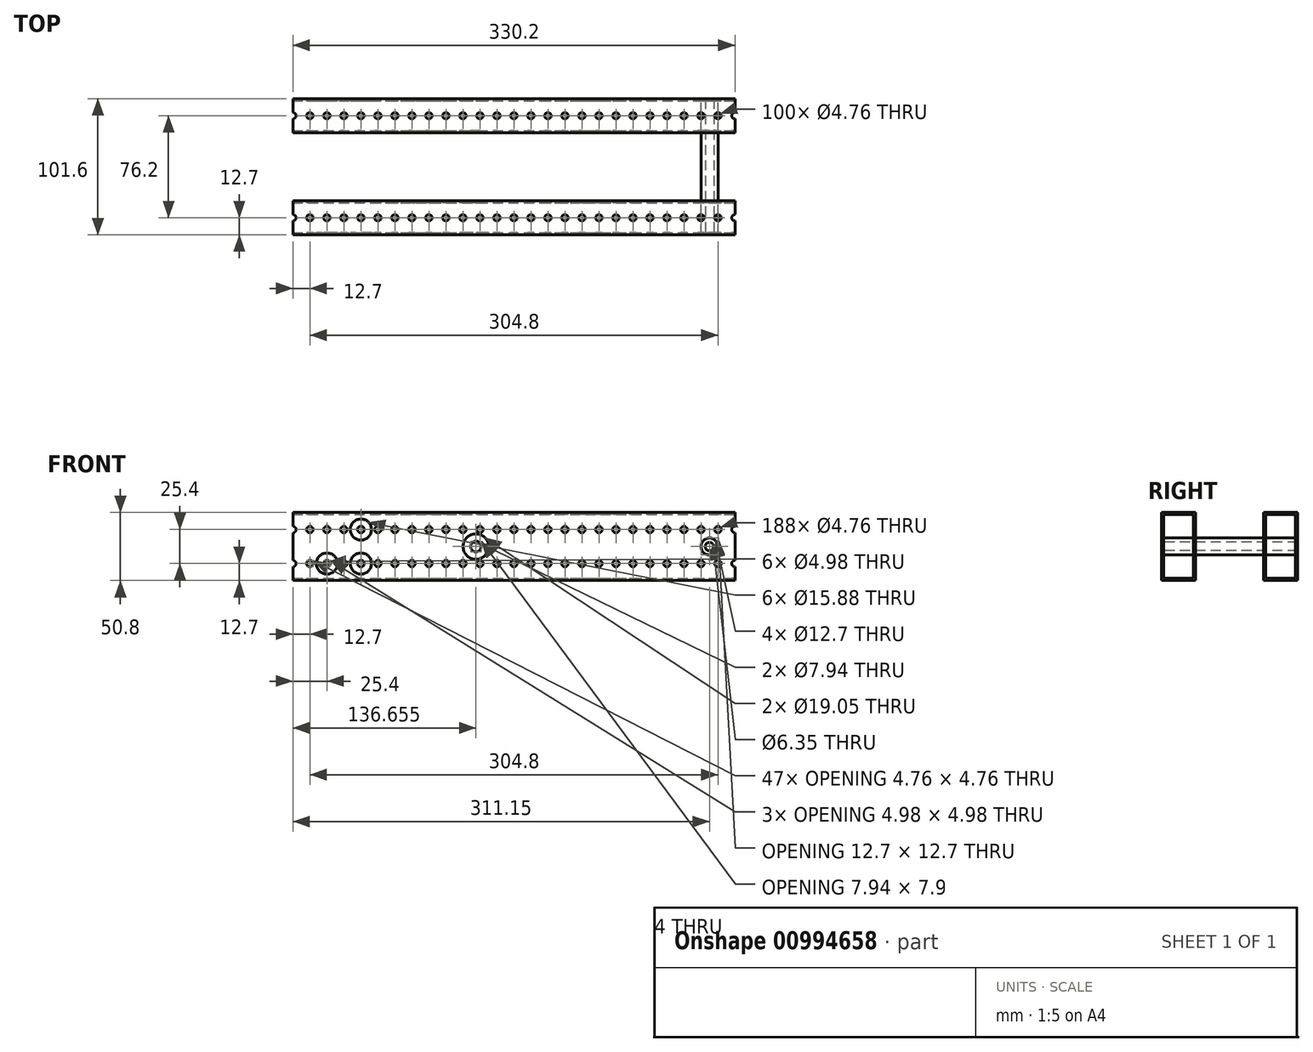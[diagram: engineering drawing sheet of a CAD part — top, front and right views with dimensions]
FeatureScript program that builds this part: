
annotation { "Feature Type Name" : "Feature", "Feature Type Description" : "" }
export const myFeature = defineFeature(function(context is Context, id is Id, definition is map)
    precondition{}
    {
        {
            var Q0;
            Q0=qCreatedBy(makeId("Front.planeOp"),FACE);
            var sketch = newSketch(context, id + "F0", { "sketchPlane" : qUnion([Q0])});
            skLineSegment(sketch, "E0.bottom", {"start": v(0, 0) * mm, "end": v(-330.2, 0) * mm});
            skLineSegment(sketch, "E0.top", {"start": v(0, 50.8) * mm, "end": v(-330.2, 50.8) * mm});
            skLineSegment(sketch, "E0.left", {"start": v(0, 0) * mm, "end": v(0, 50.8) * mm});
            skLineSegment(sketch, "E0.right", {"start": v(-330.2, 0) * mm, "end": v(-330.2, 50.8) * mm});
            skSolve(sketch);
        }
        {
            var Q0;
            Q0=makeQuery(id+"F0.imprint","IMPRINT",FACE,{"disambiguationData":[TD([[makeQuery(id+"F0.imprint","IMPRINT",EDGE,{"derivedFrom":sQuery(id+"F0.wireOp",EDGE,"E0.bottom")}),-1.0]])]});
            extrude(context, id + "F1", {"entities" : qUnion([Q0]), "depth" : 25.4 * mm, "offsetDistance" : 25.4 * mm});
        }
        {
            var Q0;
            Q0=makeQuery(id+"F1.opExtrude","SWEPT_FACE",FACE,{"disambiguationData":[OSD([sQuery(id+"F0.wireOp",EDGE,"E0.left")])]});
            var sketch = newSketch(context, id + "F2", { "sketchPlane" : qUnion([Q0])});
            skLineSegment(sketch, "E1.0", {"start": v(-1.59, 1.59) * mm, "end": v(-1.59, 49.21) * mm});
            skLineSegment(sketch, "E1.1", {"start": v(-23.81, 1.59) * mm, "end": v(-1.59, 1.59) * mm});
            skLineSegment(sketch, "E1.2", {"start": v(-23.81, 49.21) * mm, "end": v(-23.81, 1.59) * mm});
            skLineSegment(sketch, "E1.3", {"start": v(-1.59, 49.21) * mm, "end": v(-23.81, 49.21) * mm});
            skSolve(sketch);
        }
        {
            var Q0;
            Q0 = qSketchRegion(id + "F2", true);
            extrude(context, id + "F3", {"entities" : qUnion([Q0]), "operationType" : NewBodyOperationType.REMOVE, "endBound" : BoundingType.THROUGH_ALL, "oppositeDirection" : true, "depth" : 25.4 * mm, "offsetDistance" : 25.4 * mm});
        }
        {
            var Q0;
            Q0=makeQuery(id+"F1.opExtrude","CAP_FACE",FACE,{"disambiguationData":[OSD([sQuery(id+"F0.wireOp",EDGE,"E0.bottom"),sQuery(id+"F0.wireOp",EDGE,"E0.top"),sQuery(id+"F0.wireOp",EDGE,"E0.left"),sQuery(id+"F0.wireOp",EDGE,"E0.right")])],"isStart":false});
            var sketch = newSketch(context, id + "F4", { "sketchPlane" : qUnion([Q0])});
            skCircle(sketch, "E2", {"center": v(0, 38.1) * mm, "radius": 2.38 * mm});
            skCircle(sketch, "E3", {"center": v(0, 12.7) * mm, "radius": 2.38 * mm});
            skCircle(sketch, "E4.1.0.0", {"center": v(-12.7, 38.1) * mm, "radius": 2.38 * mm});
            skCircle(sketch, "E4.1.0.1", {"center": v(-12.7, 12.7) * mm, "radius": 2.38 * mm});
            skCircle(sketch, "E4.2.0.0", {"center": v(-25.4, 38.1) * mm, "radius": 2.38 * mm});
            skCircle(sketch, "E4.2.0.1", {"center": v(-25.4, 12.7) * mm, "radius": 2.38 * mm});
            skCircle(sketch, "E4.3.0.0", {"center": v(-38.1, 38.1) * mm, "radius": 2.38 * mm});
            skCircle(sketch, "E4.3.0.1", {"center": v(-38.1, 12.7) * mm, "radius": 2.38 * mm});
            skCircle(sketch, "E4.4.0.0", {"center": v(-50.8, 38.1) * mm, "radius": 2.38 * mm});
            skCircle(sketch, "E4.4.0.1", {"center": v(-50.8, 12.7) * mm, "radius": 2.38 * mm});
            skCircle(sketch, "E4.5.0.0", {"center": v(-63.5, 38.1) * mm, "radius": 2.38 * mm});
            skCircle(sketch, "E4.5.0.1", {"center": v(-63.5, 12.7) * mm, "radius": 2.38 * mm});
            skCircle(sketch, "E4.6.0.0", {"center": v(-76.2, 38.1) * mm, "radius": 2.38 * mm});
            skCircle(sketch, "E4.6.0.1", {"center": v(-76.2, 12.7) * mm, "radius": 2.38 * mm});
            skCircle(sketch, "E4.7.0.0", {"center": v(-88.9, 38.1) * mm, "radius": 2.38 * mm});
            skCircle(sketch, "E4.7.0.1", {"center": v(-88.9, 12.7) * mm, "radius": 2.38 * mm});
            skCircle(sketch, "E4.8.0.0", {"center": v(-101.6, 38.1) * mm, "radius": 2.38 * mm});
            skCircle(sketch, "E4.8.0.1", {"center": v(-101.6, 12.7) * mm, "radius": 2.38 * mm});
            skCircle(sketch, "E4.9.0.0", {"center": v(-114.3, 38.1) * mm, "radius": 2.38 * mm});
            skCircle(sketch, "E4.9.0.1", {"center": v(-114.3, 12.7) * mm, "radius": 2.38 * mm});
            skCircle(sketch, "E4.10.0.0", {"center": v(-127, 38.1) * mm, "radius": 2.38 * mm});
            skCircle(sketch, "E4.10.0.1", {"center": v(-127, 12.7) * mm, "radius": 2.38 * mm});
            skCircle(sketch, "E4.11.0.0", {"center": v(-139.7, 38.1) * mm, "radius": 2.38 * mm});
            skCircle(sketch, "E4.11.0.1", {"center": v(-139.7, 12.7) * mm, "radius": 2.38 * mm});
            skCircle(sketch, "E4.12.0.0", {"center": v(-152.4, 38.1) * mm, "radius": 2.38 * mm});
            skCircle(sketch, "E4.12.0.1", {"center": v(-152.4, 12.7) * mm, "radius": 2.38 * mm});
            skCircle(sketch, "E4.13.0.0", {"center": v(-165.1, 38.1) * mm, "radius": 2.38 * mm});
            skCircle(sketch, "E4.13.0.1", {"center": v(-165.1, 12.7) * mm, "radius": 2.38 * mm});
            skCircle(sketch, "E4.14.0.0", {"center": v(-177.8, 38.1) * mm, "radius": 2.38 * mm});
            skCircle(sketch, "E4.14.0.1", {"center": v(-177.8, 12.7) * mm, "radius": 2.38 * mm});
            skCircle(sketch, "E4.15.0.0", {"center": v(-190.5, 38.1) * mm, "radius": 2.38 * mm});
            skCircle(sketch, "E4.15.0.1", {"center": v(-190.5, 12.7) * mm, "radius": 2.38 * mm});
            skCircle(sketch, "E4.16.0.0", {"center": v(-203.2, 38.1) * mm, "radius": 2.38 * mm});
            skCircle(sketch, "E4.16.0.1", {"center": v(-203.2, 12.7) * mm, "radius": 2.38 * mm});
            skCircle(sketch, "E4.17.0.0", {"center": v(-215.9, 38.1) * mm, "radius": 2.38 * mm});
            skCircle(sketch, "E4.17.0.1", {"center": v(-215.9, 12.7) * mm, "radius": 2.38 * mm});
            skCircle(sketch, "E4.18.0.0", {"center": v(-228.6, 38.1) * mm, "radius": 2.38 * mm});
            skCircle(sketch, "E4.18.0.1", {"center": v(-228.6, 12.7) * mm, "radius": 2.38 * mm});
            skCircle(sketch, "E4.19.0.0", {"center": v(-241.3, 38.1) * mm, "radius": 2.38 * mm});
            skCircle(sketch, "E4.19.0.1", {"center": v(-241.3, 12.7) * mm, "radius": 2.38 * mm});
            skCircle(sketch, "E4.20.0.0", {"center": v(-254, 38.1) * mm, "radius": 2.38 * mm});
            skCircle(sketch, "E4.20.0.1", {"center": v(-254, 12.7) * mm, "radius": 2.38 * mm});
            skCircle(sketch, "E4.21.0.0", {"center": v(-266.7, 38.1) * mm, "radius": 2.38 * mm});
            skCircle(sketch, "E4.21.0.1", {"center": v(-266.7, 12.7) * mm, "radius": 2.38 * mm});
            skCircle(sketch, "E4.22.0.0", {"center": v(-279.4, 38.1) * mm, "radius": 2.38 * mm});
            skCircle(sketch, "E4.22.0.1", {"center": v(-279.4, 12.7) * mm, "radius": 2.38 * mm});
            skCircle(sketch, "E4.23.0.0", {"center": v(-292.1, 38.1) * mm, "radius": 2.38 * mm});
            skCircle(sketch, "E4.23.0.1", {"center": v(-292.1, 12.7) * mm, "radius": 2.38 * mm});
            skCircle(sketch, "E4.24.0.0", {"center": v(-304.8, 38.1) * mm, "radius": 2.38 * mm});
            skCircle(sketch, "E4.24.0.1", {"center": v(-304.8, 12.7) * mm, "radius": 2.38 * mm});
            skCircle(sketch, "E4.25.0.0", {"center": v(-317.5, 38.1) * mm, "radius": 2.38 * mm});
            skCircle(sketch, "E4.25.0.1", {"center": v(-317.5, 12.7) * mm, "radius": 2.38 * mm});
            skCircle(sketch, "E4.26.0.0", {"center": v(-330.2, 38.1) * mm, "radius": 2.38 * mm});
            skCircle(sketch, "E4.26.0.1", {"center": v(-330.2, 12.7) * mm, "radius": 2.38 * mm});
            skCircle(sketch, "E4.27.0.0", {"center": v(-342.9, 38.1) * mm, "radius": 2.38 * mm});
            skCircle(sketch, "E4.27.0.1", {"center": v(-342.9, 12.7) * mm, "radius": 2.38 * mm});
            skCircle(sketch, "E4.28.0.0", {"center": v(-355.6, 38.1) * mm, "radius": 2.38 * mm});
            skCircle(sketch, "E4.28.0.1", {"center": v(-355.6, 12.7) * mm, "radius": 2.38 * mm});
            skCircle(sketch, "E4.29.0.0", {"center": v(-368.3, 38.1) * mm, "radius": 2.38 * mm});
            skCircle(sketch, "E4.29.0.1", {"center": v(-368.3, 12.7) * mm, "radius": 2.38 * mm});
            skCircle(sketch, "E4.30.0.0", {"center": v(-381, 38.1) * mm, "radius": 2.38 * mm});
            skCircle(sketch, "E4.30.0.1", {"center": v(-381, 12.7) * mm, "radius": 2.38 * mm});
            skCircle(sketch, "E4.31.0.0", {"center": v(-393.7, 38.1) * mm, "radius": 2.38 * mm});
            skCircle(sketch, "E4.31.0.1", {"center": v(-393.7, 12.7) * mm, "radius": 2.38 * mm});
            skCircle(sketch, "E4.32.0.0", {"center": v(-406.4, 38.1) * mm, "radius": 2.38 * mm});
            skCircle(sketch, "E4.32.0.1", {"center": v(-406.4, 12.7) * mm, "radius": 2.38 * mm});
            skCircle(sketch, "E4.33.0.0", {"center": v(-419.1, 38.1) * mm, "radius": 2.38 * mm});
            skCircle(sketch, "E4.33.0.1", {"center": v(-419.1, 12.7) * mm, "radius": 2.38 * mm});
            skCircle(sketch, "E4.34.0.0", {"center": v(-431.8, 38.1) * mm, "radius": 2.38 * mm});
            skCircle(sketch, "E4.34.0.1", {"center": v(-431.8, 12.7) * mm, "radius": 2.38 * mm});
            skCircle(sketch, "E4.35.0.0", {"center": v(-444.5, 38.1) * mm, "radius": 2.38 * mm});
            skCircle(sketch, "E4.35.0.1", {"center": v(-444.5, 12.7) * mm, "radius": 2.38 * mm});
            skCircle(sketch, "E4.36.0.0", {"center": v(-457.2, 38.1) * mm, "radius": 2.38 * mm});
            skCircle(sketch, "E4.36.0.1", {"center": v(-457.2, 12.7) * mm, "radius": 2.38 * mm});
            skCircle(sketch, "E4.37.0.0", {"center": v(-469.9, 38.1) * mm, "radius": 2.38 * mm});
            skCircle(sketch, "E4.37.0.1", {"center": v(-469.9, 12.7) * mm, "radius": 2.38 * mm});
            skCircle(sketch, "E4.38.0.0", {"center": v(-482.6, 38.1) * mm, "radius": 2.38 * mm});
            skCircle(sketch, "E4.38.0.1", {"center": v(-482.6, 12.7) * mm, "radius": 2.38 * mm});
            skCircle(sketch, "E4.39.0.0", {"center": v(-495.3, 38.1) * mm, "radius": 2.38 * mm});
            skCircle(sketch, "E4.39.0.1", {"center": v(-495.3, 12.7) * mm, "radius": 2.38 * mm});
            skCircle(sketch, "E4.40.0.0", {"center": v(-508, 38.1) * mm, "radius": 2.38 * mm});
            skCircle(sketch, "E4.40.0.1", {"center": v(-508, 12.7) * mm, "radius": 2.38 * mm});
            skCircle(sketch, "E4.41.0.0", {"center": v(-520.7, 38.1) * mm, "radius": 2.38 * mm});
            skCircle(sketch, "E4.41.0.1", {"center": v(-520.7, 12.7) * mm, "radius": 2.38 * mm});
            skCircle(sketch, "E4.42.0.0", {"center": v(-533.4, 38.1) * mm, "radius": 2.38 * mm});
            skCircle(sketch, "E4.42.0.1", {"center": v(-533.4, 12.7) * mm, "radius": 2.38 * mm});
            skCircle(sketch, "E4.43.0.0", {"center": v(-546.1, 38.1) * mm, "radius": 2.38 * mm});
            skCircle(sketch, "E4.43.0.1", {"center": v(-546.1, 12.7) * mm, "radius": 2.38 * mm});
            skCircle(sketch, "E4.44.0.0", {"center": v(-558.8, 38.1) * mm, "radius": 2.38 * mm});
            skCircle(sketch, "E4.44.0.1", {"center": v(-558.8, 12.7) * mm, "radius": 2.38 * mm});
            skCircle(sketch, "E4.45.0.0", {"center": v(-571.5, 38.1) * mm, "radius": 2.38 * mm});
            skCircle(sketch, "E4.45.0.1", {"center": v(-571.5, 12.7) * mm, "radius": 2.38 * mm});
            skCircle(sketch, "E4.46.0.0", {"center": v(-584.2, 38.1) * mm, "radius": 2.38 * mm});
            skCircle(sketch, "E4.46.0.1", {"center": v(-584.2, 12.7) * mm, "radius": 2.38 * mm});
            skCircle(sketch, "E4.47.0.0", {"center": v(-596.9, 38.1) * mm, "radius": 2.38 * mm});
            skCircle(sketch, "E4.47.0.1", {"center": v(-596.9, 12.7) * mm, "radius": 2.38 * mm});
            skCircle(sketch, "E4.48.0.0", {"center": v(-609.6, 38.1) * mm, "radius": 2.38 * mm});
            skCircle(sketch, "E4.48.0.1", {"center": v(-609.6, 12.7) * mm, "radius": 2.38 * mm});
            skCircle(sketch, "E4.49.0.0", {"center": v(-622.3, 38.1) * mm, "radius": 2.38 * mm});
            skCircle(sketch, "E4.49.0.1", {"center": v(-622.3, 12.7) * mm, "radius": 2.38 * mm});
            skCircle(sketch, "E4.50.0.0", {"center": v(-635, 38.1) * mm, "radius": 2.38 * mm});
            skCircle(sketch, "E4.50.0.1", {"center": v(-635, 12.7) * mm, "radius": 2.38 * mm});
            skCircle(sketch, "E4.51.0.0", {"center": v(-647.7, 38.1) * mm, "radius": 2.38 * mm});
            skCircle(sketch, "E4.51.0.1", {"center": v(-647.7, 12.7) * mm, "radius": 2.38 * mm});
            skCircle(sketch, "E4.52.0.0", {"center": v(-660.4, 38.1) * mm, "radius": 2.38 * mm});
            skCircle(sketch, "E4.52.0.1", {"center": v(-660.4, 12.7) * mm, "radius": 2.38 * mm});
            skCircle(sketch, "E4.53.0.0", {"center": v(-673.1, 38.1) * mm, "radius": 2.38 * mm});
            skCircle(sketch, "E4.53.0.1", {"center": v(-673.1, 12.7) * mm, "radius": 2.38 * mm});
            skCircle(sketch, "E4.54.0.0", {"center": v(-685.8, 38.1) * mm, "radius": 2.38 * mm});
            skCircle(sketch, "E4.54.0.1", {"center": v(-685.8, 12.7) * mm, "radius": 2.38 * mm});
            skCircle(sketch, "E4.55.0.0", {"center": v(-698.5, 38.1) * mm, "radius": 2.38 * mm});
            skCircle(sketch, "E4.55.0.1", {"center": v(-698.5, 12.7) * mm, "radius": 2.38 * mm});
            skCircle(sketch, "E4.56.0.0", {"center": v(-711.2, 38.1) * mm, "radius": 2.38 * mm});
            skCircle(sketch, "E4.56.0.1", {"center": v(-711.2, 12.7) * mm, "radius": 2.38 * mm});
            skCircle(sketch, "E4.57.0.0", {"center": v(-723.9, 38.1) * mm, "radius": 2.38 * mm});
            skCircle(sketch, "E4.57.0.1", {"center": v(-723.9, 12.7) * mm, "radius": 2.38 * mm});
            skCircle(sketch, "E4.58.0.0", {"center": v(-736.6, 38.1) * mm, "radius": 2.38 * mm});
            skCircle(sketch, "E4.58.0.1", {"center": v(-736.6, 12.7) * mm, "radius": 2.38 * mm});
            skCircle(sketch, "E4.59.0.0", {"center": v(-749.3, 38.1) * mm, "radius": 2.38 * mm});
            skCircle(sketch, "E4.59.0.1", {"center": v(-749.3, 12.7) * mm, "radius": 2.38 * mm});
            skCircle(sketch, "E4.60.0.0", {"center": v(-762, 38.1) * mm, "radius": 2.38 * mm});
            skCircle(sketch, "E4.60.0.1", {"center": v(-762, 12.7) * mm, "radius": 2.38 * mm});
            skCircle(sketch, "E4.61.0.0", {"center": v(-774.7, 38.1) * mm, "radius": 2.38 * mm});
            skCircle(sketch, "E4.61.0.1", {"center": v(-774.7, 12.7) * mm, "radius": 2.38 * mm});
            skCircle(sketch, "E4.62.0.0", {"center": v(-787.4, 38.1) * mm, "radius": 2.38 * mm});
            skCircle(sketch, "E4.62.0.1", {"center": v(-787.4, 12.7) * mm, "radius": 2.38 * mm});
            skCircle(sketch, "E4.63.0.0", {"center": v(-800.1, 38.1) * mm, "radius": 2.38 * mm});
            skCircle(sketch, "E4.63.0.1", {"center": v(-800.1, 12.7) * mm, "radius": 2.38 * mm});
            skCircle(sketch, "E4.64.0.0", {"center": v(-812.8, 38.1) * mm, "radius": 2.38 * mm});
            skCircle(sketch, "E4.64.0.1", {"center": v(-812.8, 12.7) * mm, "radius": 2.38 * mm});
            skCircle(sketch, "E4.65.0.0", {"center": v(-825.5, 38.1) * mm, "radius": 2.38 * mm});
            skCircle(sketch, "E4.65.0.1", {"center": v(-825.5, 12.7) * mm, "radius": 2.38 * mm});
            skCircle(sketch, "E4.66.0.0", {"center": v(-838.2, 38.1) * mm, "radius": 2.38 * mm});
            skCircle(sketch, "E4.66.0.1", {"center": v(-838.2, 12.7) * mm, "radius": 2.38 * mm});
            skCircle(sketch, "E4.67.0.0", {"center": v(-850.9, 38.1) * mm, "radius": 2.38 * mm});
            skCircle(sketch, "E4.67.0.1", {"center": v(-850.9, 12.7) * mm, "radius": 2.38 * mm});
            skCircle(sketch, "E4.68.0.0", {"center": v(-863.6, 38.1) * mm, "radius": 2.38 * mm});
            skCircle(sketch, "E4.68.0.1", {"center": v(-863.6, 12.7) * mm, "radius": 2.38 * mm});
            skCircle(sketch, "E4.69.0.0", {"center": v(-876.3, 38.1) * mm, "radius": 2.38 * mm});
            skCircle(sketch, "E4.69.0.1", {"center": v(-876.3, 12.7) * mm, "radius": 2.38 * mm});
            skCircle(sketch, "E4.70.0.0", {"center": v(-889, 38.1) * mm, "radius": 2.38 * mm});
            skCircle(sketch, "E4.70.0.1", {"center": v(-889, 12.7) * mm, "radius": 2.38 * mm});
            skCircle(sketch, "E4.71.0.0", {"center": v(-901.7, 38.1) * mm, "radius": 2.38 * mm});
            skCircle(sketch, "E4.71.0.1", {"center": v(-901.7, 12.7) * mm, "radius": 2.38 * mm});
            skCircle(sketch, "E4.72.0.0", {"center": v(-914.4, 38.1) * mm, "radius": 2.38 * mm});
            skCircle(sketch, "E4.72.0.1", {"center": v(-914.4, 12.7) * mm, "radius": 2.38 * mm});
            skCircle(sketch, "E4.73.0.0", {"center": v(-927.1, 38.1) * mm, "radius": 2.38 * mm});
            skCircle(sketch, "E4.73.0.1", {"center": v(-927.1, 12.7) * mm, "radius": 2.38 * mm});
            skCircle(sketch, "E4.74.0.0", {"center": v(-939.8, 38.1) * mm, "radius": 2.38 * mm});
            skCircle(sketch, "E4.74.0.1", {"center": v(-939.8, 12.7) * mm, "radius": 2.38 * mm});
            skCircle(sketch, "E4.75.0.0", {"center": v(-952.5, 38.1) * mm, "radius": 2.38 * mm});
            skCircle(sketch, "E4.75.0.1", {"center": v(-952.5, 12.7) * mm, "radius": 2.38 * mm});
            skCircle(sketch, "E4.76.0.0", {"center": v(-965.2, 38.1) * mm, "radius": 2.38 * mm});
            skCircle(sketch, "E4.76.0.1", {"center": v(-965.2, 12.7) * mm, "radius": 2.38 * mm});
            skCircle(sketch, "E4.77.0.0", {"center": v(-977.9, 38.1) * mm, "radius": 2.38 * mm});
            skCircle(sketch, "E4.77.0.1", {"center": v(-977.9, 12.7) * mm, "radius": 2.38 * mm});
            skCircle(sketch, "E4.78.0.0", {"center": v(-990.6, 38.1) * mm, "radius": 2.38 * mm});
            skCircle(sketch, "E4.78.0.1", {"center": v(-990.6, 12.7) * mm, "radius": 2.38 * mm});
            skCircle(sketch, "E4.79.0.0", {"center": v(-1003.3, 38.1) * mm, "radius": 2.38 * mm});
            skCircle(sketch, "E4.79.0.1", {"center": v(-1003.3, 12.7) * mm, "radius": 2.38 * mm});
            skCircle(sketch, "E4.80.0.0", {"center": v(-1016, 38.1) * mm, "radius": 2.38 * mm});
            skCircle(sketch, "E4.80.0.1", {"center": v(-1016, 12.7) * mm, "radius": 2.38 * mm});
            skCircle(sketch, "E4.81.0.0", {"center": v(-1028.7, 38.1) * mm, "radius": 2.38 * mm});
            skCircle(sketch, "E4.81.0.1", {"center": v(-1028.7, 12.7) * mm, "radius": 2.38 * mm});
            skCircle(sketch, "E4.82.0.0", {"center": v(-1041.4, 38.1) * mm, "radius": 2.38 * mm});
            skCircle(sketch, "E4.82.0.1", {"center": v(-1041.4, 12.7) * mm, "radius": 2.38 * mm});
            skCircle(sketch, "E4.83.0.0", {"center": v(-1054.1, 38.1) * mm, "radius": 2.38 * mm});
            skCircle(sketch, "E4.83.0.1", {"center": v(-1054.1, 12.7) * mm, "radius": 2.38 * mm});
            skCircle(sketch, "E4.84.0.0", {"center": v(-1066.8, 38.1) * mm, "radius": 2.38 * mm});
            skCircle(sketch, "E4.84.0.1", {"center": v(-1066.8, 12.7) * mm, "radius": 2.38 * mm});
            skCircle(sketch, "E4.85.0.0", {"center": v(-1079.5, 38.1) * mm, "radius": 2.38 * mm});
            skCircle(sketch, "E4.85.0.1", {"center": v(-1079.5, 12.7) * mm, "radius": 2.38 * mm});
            skCircle(sketch, "E4.86.0.0", {"center": v(-1092.2, 38.1) * mm, "radius": 2.38 * mm});
            skCircle(sketch, "E4.86.0.1", {"center": v(-1092.2, 12.7) * mm, "radius": 2.38 * mm});
            skCircle(sketch, "E4.87.0.0", {"center": v(-1104.9, 38.1) * mm, "radius": 2.38 * mm});
            skCircle(sketch, "E4.87.0.1", {"center": v(-1104.9, 12.7) * mm, "radius": 2.38 * mm});
            skCircle(sketch, "E4.88.0.0", {"center": v(-1117.6, 38.1) * mm, "radius": 2.38 * mm});
            skCircle(sketch, "E4.88.0.1", {"center": v(-1117.6, 12.7) * mm, "radius": 2.38 * mm});
            skCircle(sketch, "E4.89.0.0", {"center": v(-1130.3, 38.1) * mm, "radius": 2.38 * mm});
            skCircle(sketch, "E4.89.0.1", {"center": v(-1130.3, 12.7) * mm, "radius": 2.38 * mm});
            skCircle(sketch, "E4.90.0.0", {"center": v(-1143, 38.1) * mm, "radius": 2.38 * mm});
            skCircle(sketch, "E4.90.0.1", {"center": v(-1143, 12.7) * mm, "radius": 2.38 * mm});
            skCircle(sketch, "E4.91.0.0", {"center": v(-1155.7, 38.1) * mm, "radius": 2.38 * mm});
            skCircle(sketch, "E4.91.0.1", {"center": v(-1155.7, 12.7) * mm, "radius": 2.38 * mm});
            skCircle(sketch, "E4.92.0.0", {"center": v(-1168.4, 38.1) * mm, "radius": 2.38 * mm});
            skCircle(sketch, "E4.92.0.1", {"center": v(-1168.4, 12.7) * mm, "radius": 2.38 * mm});
            skCircle(sketch, "E4.93.0.0", {"center": v(-1181.1, 38.1) * mm, "radius": 2.38 * mm});
            skCircle(sketch, "E4.93.0.1", {"center": v(-1181.1, 12.7) * mm, "radius": 2.38 * mm});
            skCircle(sketch, "E4.94.0.0", {"center": v(-1193.8, 38.1) * mm, "radius": 2.38 * mm});
            skCircle(sketch, "E4.94.0.1", {"center": v(-1193.8, 12.7) * mm, "radius": 2.38 * mm});
            skCircle(sketch, "E4.95.0.0", {"center": v(-1206.5, 38.1) * mm, "radius": 2.38 * mm});
            skCircle(sketch, "E4.95.0.1", {"center": v(-1206.5, 12.7) * mm, "radius": 2.38 * mm});
            skCircle(sketch, "E4.96.0.0", {"center": v(-1219.2, 38.1) * mm, "radius": 2.38 * mm});
            skCircle(sketch, "E4.96.0.1", {"center": v(-1219.2, 12.7) * mm, "radius": 2.38 * mm});
            skCircle(sketch, "E4.97.0.0", {"center": v(-1231.9, 38.1) * mm, "radius": 2.38 * mm});
            skCircle(sketch, "E4.97.0.1", {"center": v(-1231.9, 12.7) * mm, "radius": 2.38 * mm});
            skCircle(sketch, "E4.98.0.0", {"center": v(-1244.6, 38.1) * mm, "radius": 2.38 * mm});
            skCircle(sketch, "E4.98.0.1", {"center": v(-1244.6, 12.7) * mm, "radius": 2.38 * mm});
            skCircle(sketch, "E4.99.0.0", {"center": v(-1257.3, 38.1) * mm, "radius": 2.38 * mm});
            skCircle(sketch, "E4.99.0.1", {"center": v(-1257.3, 12.7) * mm, "radius": 2.38 * mm});
            skLineSegment(sketch, "E4.direction1", {"start": v(0, 12.7) * mm, "end": v(-12.7, 12.7) * mm, "construction": true});
            skSolve(sketch);
        }
        {
            var Q0;
            Q0 = qSketchRegion(id + "F4", true);
            extrude(context, id + "F5", {"entities" : qUnion([Q0]), "operationType" : NewBodyOperationType.REMOVE, "endBound" : BoundingType.THROUGH_ALL, "oppositeDirection" : true, "depth" : 25.4 * mm, "offsetDistance" : 25.4 * mm});
        }
        {
            var Q0;
            Q0=makeQuery(id+"F1.opExtrude","SWEPT_FACE",FACE,{"disambiguationData":[OSD([sQuery(id+"F0.wireOp",EDGE,"E0.top")])]});
            var sketch = newSketch(context, id + "F6", { "sketchPlane" : qUnion([Q0])});
            skCircle(sketch, "E5", {"center": v(0, -12.7) * mm, "radius": 2.38 * mm});
            skCircle(sketch, "E6.1.0.0", {"center": v(-12.7, -12.7) * mm, "radius": 2.38 * mm});
            skCircle(sketch, "E6.2.0.0", {"center": v(-25.4, -12.7) * mm, "radius": 2.38 * mm});
            skCircle(sketch, "E6.3.0.0", {"center": v(-38.1, -12.7) * mm, "radius": 2.38 * mm});
            skCircle(sketch, "E6.4.0.0", {"center": v(-50.8, -12.7) * mm, "radius": 2.38 * mm});
            skCircle(sketch, "E6.5.0.0", {"center": v(-63.5, -12.7) * mm, "radius": 2.38 * mm});
            skCircle(sketch, "E6.6.0.0", {"center": v(-76.2, -12.7) * mm, "radius": 2.38 * mm});
            skCircle(sketch, "E6.7.0.0", {"center": v(-88.9, -12.7) * mm, "radius": 2.38 * mm});
            skCircle(sketch, "E6.8.0.0", {"center": v(-101.6, -12.7) * mm, "radius": 2.38 * mm});
            skCircle(sketch, "E6.9.0.0", {"center": v(-114.3, -12.7) * mm, "radius": 2.38 * mm});
            skCircle(sketch, "E6.10.0.0", {"center": v(-127, -12.7) * mm, "radius": 2.38 * mm});
            skCircle(sketch, "E6.11.0.0", {"center": v(-139.7, -12.7) * mm, "radius": 2.38 * mm});
            skCircle(sketch, "E6.12.0.0", {"center": v(-152.4, -12.7) * mm, "radius": 2.38 * mm});
            skCircle(sketch, "E6.13.0.0", {"center": v(-165.1, -12.7) * mm, "radius": 2.38 * mm});
            skCircle(sketch, "E6.14.0.0", {"center": v(-177.8, -12.7) * mm, "radius": 2.38 * mm});
            skCircle(sketch, "E6.15.0.0", {"center": v(-190.5, -12.7) * mm, "radius": 2.38 * mm});
            skCircle(sketch, "E6.16.0.0", {"center": v(-203.2, -12.7) * mm, "radius": 2.38 * mm});
            skCircle(sketch, "E6.17.0.0", {"center": v(-215.9, -12.7) * mm, "radius": 2.38 * mm});
            skCircle(sketch, "E6.18.0.0", {"center": v(-228.6, -12.7) * mm, "radius": 2.38 * mm});
            skCircle(sketch, "E6.19.0.0", {"center": v(-241.3, -12.7) * mm, "radius": 2.38 * mm});
            skCircle(sketch, "E6.20.0.0", {"center": v(-254, -12.7) * mm, "radius": 2.38 * mm});
            skCircle(sketch, "E6.21.0.0", {"center": v(-266.7, -12.7) * mm, "radius": 2.38 * mm});
            skCircle(sketch, "E6.22.0.0", {"center": v(-279.4, -12.7) * mm, "radius": 2.38 * mm});
            skCircle(sketch, "E6.23.0.0", {"center": v(-292.1, -12.7) * mm, "radius": 2.38 * mm});
            skCircle(sketch, "E6.24.0.0", {"center": v(-304.8, -12.7) * mm, "radius": 2.38 * mm});
            skCircle(sketch, "E6.25.0.0", {"center": v(-317.5, -12.7) * mm, "radius": 2.38 * mm});
            skCircle(sketch, "E6.26.0.0", {"center": v(-330.2, -12.7) * mm, "radius": 2.38 * mm});
            skCircle(sketch, "E6.27.0.0", {"center": v(-342.9, -12.7) * mm, "radius": 2.38 * mm});
            skCircle(sketch, "E6.28.0.0", {"center": v(-355.6, -12.7) * mm, "radius": 2.38 * mm});
            skCircle(sketch, "E6.29.0.0", {"center": v(-368.3, -12.7) * mm, "radius": 2.38 * mm});
            skCircle(sketch, "E6.30.0.0", {"center": v(-381, -12.7) * mm, "radius": 2.38 * mm});
            skCircle(sketch, "E6.31.0.0", {"center": v(-393.7, -12.7) * mm, "radius": 2.38 * mm});
            skCircle(sketch, "E6.32.0.0", {"center": v(-406.4, -12.7) * mm, "radius": 2.38 * mm});
            skCircle(sketch, "E6.33.0.0", {"center": v(-419.1, -12.7) * mm, "radius": 2.38 * mm});
            skCircle(sketch, "E6.34.0.0", {"center": v(-431.8, -12.7) * mm, "radius": 2.38 * mm});
            skCircle(sketch, "E6.35.0.0", {"center": v(-444.5, -12.7) * mm, "radius": 2.38 * mm});
            skCircle(sketch, "E6.36.0.0", {"center": v(-457.2, -12.7) * mm, "radius": 2.38 * mm});
            skCircle(sketch, "E6.37.0.0", {"center": v(-469.9, -12.7) * mm, "radius": 2.38 * mm});
            skCircle(sketch, "E6.38.0.0", {"center": v(-482.6, -12.7) * mm, "radius": 2.38 * mm});
            skCircle(sketch, "E6.39.0.0", {"center": v(-495.3, -12.7) * mm, "radius": 2.38 * mm});
            skCircle(sketch, "E6.40.0.0", {"center": v(-508, -12.7) * mm, "radius": 2.38 * mm});
            skCircle(sketch, "E6.41.0.0", {"center": v(-520.7, -12.7) * mm, "radius": 2.38 * mm});
            skCircle(sketch, "E6.42.0.0", {"center": v(-533.4, -12.7) * mm, "radius": 2.38 * mm});
            skCircle(sketch, "E6.43.0.0", {"center": v(-546.1, -12.7) * mm, "radius": 2.38 * mm});
            skCircle(sketch, "E6.44.0.0", {"center": v(-558.8, -12.7) * mm, "radius": 2.38 * mm});
            skCircle(sketch, "E6.45.0.0", {"center": v(-571.5, -12.7) * mm, "radius": 2.38 * mm});
            skCircle(sketch, "E6.46.0.0", {"center": v(-584.2, -12.7) * mm, "radius": 2.38 * mm});
            skCircle(sketch, "E6.47.0.0", {"center": v(-596.9, -12.7) * mm, "radius": 2.38 * mm});
            skCircle(sketch, "E6.48.0.0", {"center": v(-609.6, -12.7) * mm, "radius": 2.38 * mm});
            skCircle(sketch, "E6.49.0.0", {"center": v(-622.3, -12.7) * mm, "radius": 2.38 * mm});
            skCircle(sketch, "E6.50.0.0", {"center": v(-635, -12.7) * mm, "radius": 2.38 * mm});
            skCircle(sketch, "E6.51.0.0", {"center": v(-647.7, -12.7) * mm, "radius": 2.38 * mm});
            skCircle(sketch, "E6.52.0.0", {"center": v(-660.4, -12.7) * mm, "radius": 2.38 * mm});
            skCircle(sketch, "E6.53.0.0", {"center": v(-673.1, -12.7) * mm, "radius": 2.38 * mm});
            skCircle(sketch, "E6.54.0.0", {"center": v(-685.8, -12.7) * mm, "radius": 2.38 * mm});
            skCircle(sketch, "E6.55.0.0", {"center": v(-698.5, -12.7) * mm, "radius": 2.38 * mm});
            skCircle(sketch, "E6.56.0.0", {"center": v(-711.2, -12.7) * mm, "radius": 2.38 * mm});
            skCircle(sketch, "E6.57.0.0", {"center": v(-723.9, -12.7) * mm, "radius": 2.38 * mm});
            skCircle(sketch, "E6.58.0.0", {"center": v(-736.6, -12.7) * mm, "radius": 2.38 * mm});
            skCircle(sketch, "E6.59.0.0", {"center": v(-749.3, -12.7) * mm, "radius": 2.38 * mm});
            skCircle(sketch, "E6.60.0.0", {"center": v(-762, -12.7) * mm, "radius": 2.38 * mm});
            skCircle(sketch, "E6.61.0.0", {"center": v(-774.7, -12.7) * mm, "radius": 2.38 * mm});
            skCircle(sketch, "E6.62.0.0", {"center": v(-787.4, -12.7) * mm, "radius": 2.38 * mm});
            skCircle(sketch, "E6.63.0.0", {"center": v(-800.1, -12.7) * mm, "radius": 2.38 * mm});
            skCircle(sketch, "E6.64.0.0", {"center": v(-812.8, -12.7) * mm, "radius": 2.38 * mm});
            skCircle(sketch, "E6.65.0.0", {"center": v(-825.5, -12.7) * mm, "radius": 2.38 * mm});
            skCircle(sketch, "E6.66.0.0", {"center": v(-838.2, -12.7) * mm, "radius": 2.38 * mm});
            skCircle(sketch, "E6.67.0.0", {"center": v(-850.9, -12.7) * mm, "radius": 2.38 * mm});
            skCircle(sketch, "E6.68.0.0", {"center": v(-863.6, -12.7) * mm, "radius": 2.38 * mm});
            skCircle(sketch, "E6.69.0.0", {"center": v(-876.3, -12.7) * mm, "radius": 2.38 * mm});
            skCircle(sketch, "E6.70.0.0", {"center": v(-889, -12.7) * mm, "radius": 2.38 * mm});
            skCircle(sketch, "E6.71.0.0", {"center": v(-901.7, -12.7) * mm, "radius": 2.38 * mm});
            skCircle(sketch, "E6.72.0.0", {"center": v(-914.4, -12.7) * mm, "radius": 2.38 * mm});
            skCircle(sketch, "E6.73.0.0", {"center": v(-927.1, -12.7) * mm, "radius": 2.38 * mm});
            skCircle(sketch, "E6.74.0.0", {"center": v(-939.8, -12.7) * mm, "radius": 2.38 * mm});
            skCircle(sketch, "E6.75.0.0", {"center": v(-952.5, -12.7) * mm, "radius": 2.38 * mm});
            skCircle(sketch, "E6.76.0.0", {"center": v(-965.2, -12.7) * mm, "radius": 2.38 * mm});
            skCircle(sketch, "E6.77.0.0", {"center": v(-977.9, -12.7) * mm, "radius": 2.38 * mm});
            skCircle(sketch, "E6.78.0.0", {"center": v(-990.6, -12.7) * mm, "radius": 2.38 * mm});
            skCircle(sketch, "E6.79.0.0", {"center": v(-1003.3, -12.7) * mm, "radius": 2.38 * mm});
            skCircle(sketch, "E6.80.0.0", {"center": v(-1016, -12.7) * mm, "radius": 2.38 * mm});
            skCircle(sketch, "E6.81.0.0", {"center": v(-1028.7, -12.7) * mm, "radius": 2.38 * mm});
            skCircle(sketch, "E6.82.0.0", {"center": v(-1041.4, -12.7) * mm, "radius": 2.38 * mm});
            skCircle(sketch, "E6.83.0.0", {"center": v(-1054.1, -12.7) * mm, "radius": 2.38 * mm});
            skCircle(sketch, "E6.84.0.0", {"center": v(-1066.8, -12.7) * mm, "radius": 2.38 * mm});
            skCircle(sketch, "E6.85.0.0", {"center": v(-1079.5, -12.7) * mm, "radius": 2.38 * mm});
            skCircle(sketch, "E6.86.0.0", {"center": v(-1092.2, -12.7) * mm, "radius": 2.38 * mm});
            skCircle(sketch, "E6.87.0.0", {"center": v(-1104.9, -12.7) * mm, "radius": 2.38 * mm});
            skCircle(sketch, "E6.88.0.0", {"center": v(-1117.6, -12.7) * mm, "radius": 2.38 * mm});
            skCircle(sketch, "E6.89.0.0", {"center": v(-1130.3, -12.7) * mm, "radius": 2.38 * mm});
            skCircle(sketch, "E6.90.0.0", {"center": v(-1143, -12.7) * mm, "radius": 2.38 * mm});
            skCircle(sketch, "E6.91.0.0", {"center": v(-1155.7, -12.7) * mm, "radius": 2.38 * mm});
            skCircle(sketch, "E6.92.0.0", {"center": v(-1168.4, -12.7) * mm, "radius": 2.38 * mm});
            skCircle(sketch, "E6.93.0.0", {"center": v(-1181.1, -12.7) * mm, "radius": 2.38 * mm});
            skCircle(sketch, "E6.94.0.0", {"center": v(-1193.8, -12.7) * mm, "radius": 2.38 * mm});
            skCircle(sketch, "E6.95.0.0", {"center": v(-1206.5, -12.7) * mm, "radius": 2.38 * mm});
            skCircle(sketch, "E6.96.0.0", {"center": v(-1219.2, -12.7) * mm, "radius": 2.38 * mm});
            skCircle(sketch, "E6.97.0.0", {"center": v(-1231.9, -12.7) * mm, "radius": 2.38 * mm});
            skCircle(sketch, "E6.98.0.0", {"center": v(-1244.6, -12.7) * mm, "radius": 2.38 * mm});
            skCircle(sketch, "E6.99.0.0", {"center": v(-1257.3, -12.7) * mm, "radius": 2.38 * mm});
            skLineSegment(sketch, "E6.direction1", {"start": v(0, -12.7) * mm, "end": v(-12.7, -12.7) * mm, "construction": true});
            skSolve(sketch);
        }
        {
            var Q0;
            Q0 = qSketchRegion(id + "F6", true);
            extrude(context, id + "F7", {"entities" : qUnion([Q0]), "operationType" : NewBodyOperationType.REMOVE, "endBound" : BoundingType.THROUGH_ALL, "oppositeDirection" : true, "depth" : 25.4 * mm, "offsetDistance" : 25.4 * mm});
        }
        {
            var Q0;
            Q0=makeQuery(id+"F1.opExtrude","CAP_FACE",FACE,{"disambiguationData":[OSD([sQuery(id+"F0.wireOp",EDGE,"E0.bottom"),sQuery(id+"F0.wireOp",EDGE,"E0.top"),sQuery(id+"F0.wireOp",EDGE,"E0.left"),sQuery(id+"F0.wireOp",EDGE,"E0.right")])],"isStart":false});
            var sketch = newSketch(context, id + "F8", { "sketchPlane" : qUnion([Q0])});
            skCircle(sketch, "E7", {"center": v(-19.05, 25.4) * mm, "radius": 6.35 * mm});
            skPoint(sketch, "E7.centerSnap0", {"position": v(0, 25.4) * mm});
            skCircle(sketch, "E8", {"center": v(-193.54, 25.4) * mm, "radius": 3.97 * mm});
            skSolve(sketch);
        }
        {
            var Q0;
            Q0=makeQuery(id+"F8.imprint","IMPRINT",FACE,{"disambiguationData":[TD([[makeQuery(id+"F8.imprint","IMPRINT",EDGE,{"derivedFrom":sQuery(id+"F8.wireOp",EDGE,"E7")}),1.0]])]});
            var Q1;
            Q1=makeQuery(id+"F8.imprint","IMPRINT",FACE,{"disambiguationData":[TD([[makeQuery(id+"F8.imprint","IMPRINT",EDGE,{"derivedFrom":sQuery(id+"F8.wireOp",EDGE,"E8")}),1.0]])]});
            extrude(context, id + "F9", {"entities" : qUnion([Q0, Q1]), "operationType" : NewBodyOperationType.REMOVE, "endBound" : BoundingType.THROUGH_ALL, "oppositeDirection" : true, "depth" : 25.4 * mm, "offsetDistance" : 25.4 * mm});
        }
        {
            var Q0;
            Q0=makeQuery(id+"F1.opExtrude","CAP_FACE",FACE,{"disambiguationData":[OSD([sQuery(id+"F0.wireOp",EDGE,"E0.bottom"),sQuery(id+"F0.wireOp",EDGE,"E0.top"),sQuery(id+"F0.wireOp",EDGE,"E0.left"),sQuery(id+"F0.wireOp",EDGE,"E0.right")])],"isStart":false});
            var sketch = newSketch(context, id + "F10", { "sketchPlane" : qUnion([Q0])});
            skCircle(sketch, "E9", {"center": v(-193.54, 25.4) * mm, "radius": 9.53 * mm});
            skSolve(sketch);
        }
        {
            var Q0;
            Q0=makeQuery(id+"F10.imprint","IMPRINT",FACE,{"disambiguationData":[TD([[makeQuery(id+"F10.imprint","IMPRINT",EDGE,{"derivedFrom":sQuery(id+"F10.wireOp",EDGE,"E9")}),1.0]])]});
            extrude(context, id + "F11", {"entities" : qUnion([Q0]), "operationType" : NewBodyOperationType.REMOVE, "oppositeDirection" : true, "depth" : 12.7 * mm, "offsetDistance" : 25.4 * mm});
        }
        {
            var Q0;
            Q0=qCreatedBy(makeId("Front.planeOp"),FACE);
            cPlane(context, id + "F12", {"entities" : qUnion([Q0]), "cplaneType" : CPlaneType.OFFSET, "offset" : 25.4 * mm, "oppositeDirection" : true, "width" : 152.4 * mm, "height" : 152.4 * mm});
        }
        {
            var Q0;
            Q0=makeQuery(id+"F1.opExtrude","CAP_FACE",FACE,{"disambiguationData":[OSD([sQuery(id+"F0.wireOp",EDGE,"E0.bottom"),sQuery(id+"F0.wireOp",EDGE,"E0.top"),sQuery(id+"F0.wireOp",EDGE,"E0.left"),sQuery(id+"F0.wireOp",EDGE,"E0.right")])],"isStart":false});
            var sketch = newSketch(context, id + "F13", { "sketchPlane" : qUnion([Q0])});
            skCircle(sketch, "E10", {"center": v(-304.8, 12.7) * mm, "radius": 2.49 * mm});
            skCircle(sketch, "E11", {"center": v(-279.4, 38.1) * mm, "radius": 2.49 * mm});
            skCircle(sketch, "E12", {"center": v(-279.4, 12.7) * mm, "radius": 2.49 * mm});
            skSolve(sketch);
        }
        {
            var Q0;
            Q0 = qSketchRegion(id + "F13", true);
            extrude(context, id + "F14", {"entities" : qUnion([Q0]), "operationType" : NewBodyOperationType.REMOVE, "endBound" : BoundingType.THROUGH_ALL, "oppositeDirection" : true, "depth" : 25.4 * mm, "offsetDistance" : 25.4 * mm});
        }
        {
            var Q0;
            Q0=makeQuery(id+"F1.opExtrude","CAP_FACE",FACE,{"disambiguationData":[OSD([sQuery(id+"F0.wireOp",EDGE,"E0.bottom"),sQuery(id+"F0.wireOp",EDGE,"E0.top"),sQuery(id+"F0.wireOp",EDGE,"E0.left"),sQuery(id+"F0.wireOp",EDGE,"E0.right")])],"isStart":false});
            var sketch = newSketch(context, id + "F15", { "sketchPlane" : qUnion([Q0])});
            skCircle(sketch, "E13.0", {"center": v(-304.8, 12.7) * mm, "radius": 2.49 * mm});
            skCircle(sketch, "E13.1", {"center": v(-279.4, 38.1) * mm, "radius": 2.49 * mm});
            skCircle(sketch, "E13.2", {"center": v(-279.4, 12.7) * mm, "radius": 2.49 * mm});
            skCircle(sketch, "E14", {"center": v(-304.8, 12.7) * mm, "radius": 7.94 * mm});
            skCircle(sketch, "E15", {"center": v(-279.4, 12.7) * mm, "radius": 7.94 * mm});
            skCircle(sketch, "E16", {"center": v(-279.4, 38.1) * mm, "radius": 7.94 * mm});
            skSolve(sketch);
        }
        {
            var Q0;
            Q0=makeQuery(id+"F15.imprint","IMPRINT",FACE,{"disambiguationData":[TD([[makeQuery(id+"F15.imprint","IMPRINT",EDGE,{"derivedFrom":sQuery(id+"F15.wireOp",EDGE,"E13.0")}),-1.0]])]});
            var Q1;
            Q1=makeQuery(id+"F15.imprint","IMPRINT",FACE,{"disambiguationData":[TD([[makeQuery(id+"F15.imprint","IMPRINT",EDGE,{"derivedFrom":sQuery(id+"F15.wireOp",EDGE,"E13.2")}),-1.0]])]});
            var Q2;
            Q2=makeQuery(id+"F15.imprint","IMPRINT",FACE,{"disambiguationData":[TD([[makeQuery(id+"F15.imprint","IMPRINT",EDGE,{"derivedFrom":sQuery(id+"F15.wireOp",EDGE,"E13.1")}),-1.0]])]});
            extrude(context, id + "F16", {"entities" : qUnion([Q0, Q1, Q2]), "operationType" : NewBodyOperationType.REMOVE, "oppositeDirection" : true, "depth" : 12.7 * mm, "offsetDistance" : 25.4 * mm});
        }
        {
            var Q0;
            Q0=makeQuery(id+"F1.opExtrude","SWEPT_BODY",BODY,{"disambiguationData":[OSD([sQuery(id+"F0.wireOp",EDGE,"E0.bottom"),sQuery(id+"F0.wireOp",EDGE,"E0.top"),sQuery(id+"F0.wireOp",EDGE,"E0.left"),sQuery(id+"F0.wireOp",EDGE,"E0.right")])]});
            var Q1;
            Q1=qCreatedBy(id+"F12.planeOp",FACE);
            mirror(context, id + "F17", {"entities" : qUnion([Q0]), "mirrorPlane" : qUnion([Q1])});
        }
        {
            var Q0;
            Q0=qCreatedBy(id+"F12.planeOp",FACE);
            var sketch = newSketch(context, id + "F18", { "sketchPlane" : qUnion([Q0])});
            skCircle(sketch, "E17.0", {"center": v(-19.05, 25.4) * mm, "radius": 6.35 * mm});
            skSolve(sketch);
        }
        {
            var Q0;
            Q0 = qSketchRegion(id + "F18", true);
            extrude(context, id + "F19", {"entities" : qUnion([Q0]), "depth" : 101.6 * mm, "offsetDistance" : 25.4 * mm, "symmetric" : true});
        }
        {
            var Q0;
            Q0=makeQuery(id+"F19.opExtrude","CAP_FACE",FACE,{"disambiguationData":[OSD([sQuery(id+"F18.wireOp",EDGE,"E17.0")])],"isStart":false});
            var sketch = newSketch(context, id + "F20", { "sketchPlane" : qUnion([Q0])});
            skCircle(sketch, "E18", {"center": v(-19.05, 25.4) * mm, "radius": 3.18 * mm});
            skSolve(sketch);
        }
        {
            var Q0;
            Q0=makeQuery(id+"F20.imprint","IMPRINT",FACE,{"disambiguationData":[TD([[makeQuery(id+"F20.imprint","IMPRINT",EDGE,{"derivedFrom":sQuery(id+"F20.wireOp",EDGE,"E18")}),1.0]])]});
            extrude(context, id + "F21", {"entities" : qUnion([Q0]), "operationType" : NewBodyOperationType.REMOVE, "endBound" : BoundingType.THROUGH_ALL, "oppositeDirection" : true, "depth" : 25.4 * mm, "offsetDistance" : 25.4 * mm});
        }
    });
